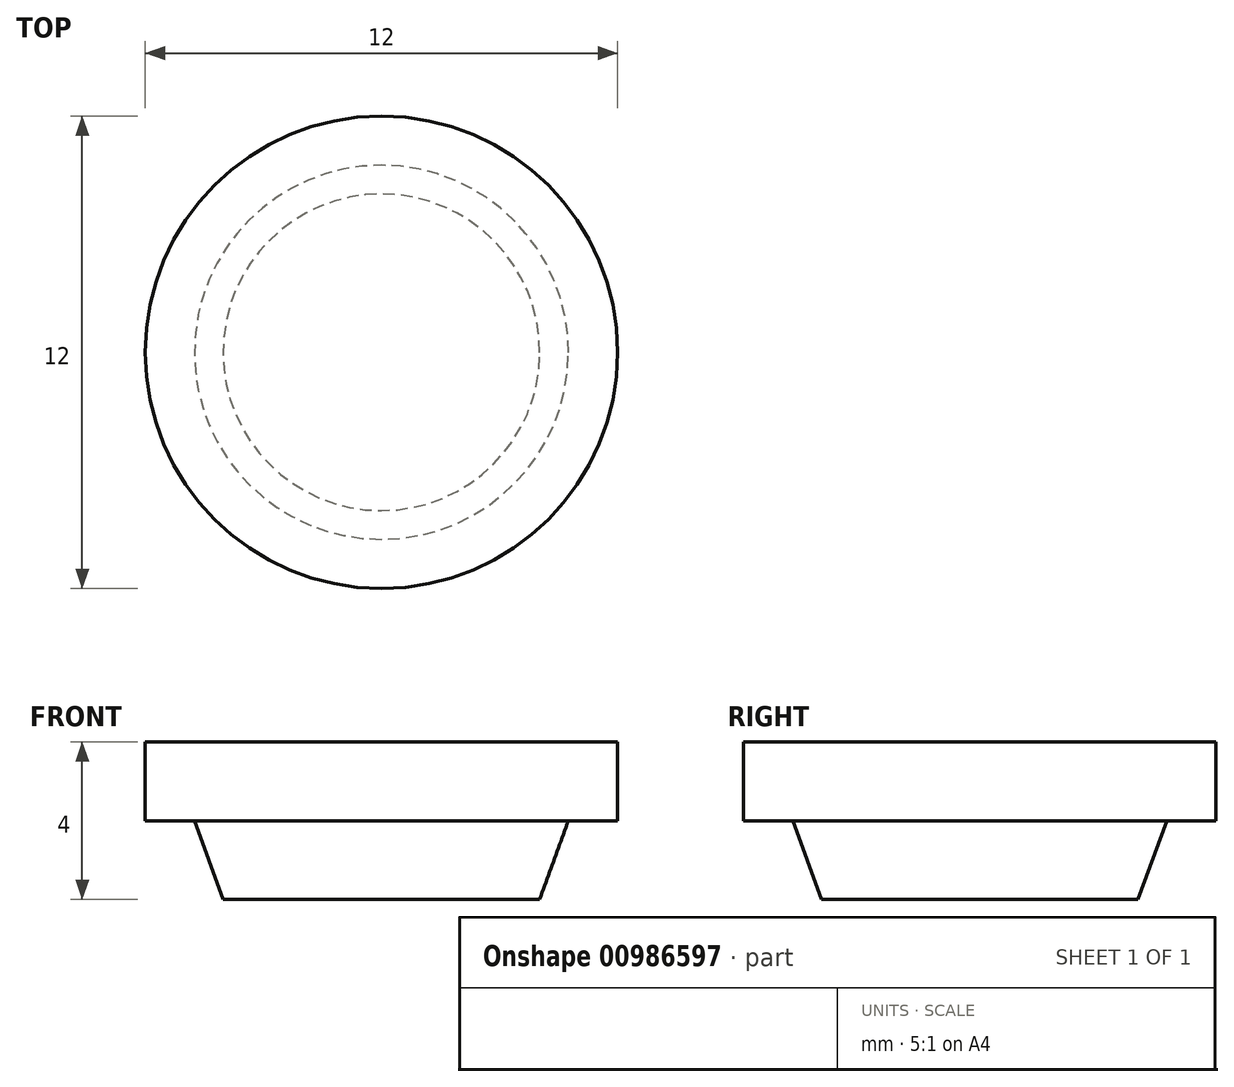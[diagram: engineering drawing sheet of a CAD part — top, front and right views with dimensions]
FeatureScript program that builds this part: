
annotation { "Feature Type Name" : "Feature", "Feature Type Description" : "" }
export const myFeature = defineFeature(function(context is Context, id is Id, definition is map)
    precondition{}
    {
        {
            var Q0;
            Q0=qCreatedBy(makeId("Top.planeOp"),FACE);
            var sketch = newSketch(context, id + "F0", { "sketchPlane" : qUnion([Q0])});
            skCircle(sketch, "E0", {"center": v(0, 0) * mm, "radius": 6 * mm});
            skSolve(sketch);
        }
        {
            var Q0;
            Q0 = qSketchRegion(id + "F0", true);
            extrude(context, id + "F1", {"entities" : qUnion([Q0]), "depth" : 2 * mm, "offsetDistance" : 25 * mm});
        }
        {
            var Q0;
            Q0=qCreatedBy(makeId("Top.planeOp"),FACE);
            var sketch = newSketch(context, id + "F2", { "sketchPlane" : qUnion([Q0])});
            skCircle(sketch, "E1", {"center": v(0, 0) * mm, "radius": 4.75 * mm});
            skSolve(sketch);
        }
        {
            var Q0;
            Q0 = qSketchRegion(id + "F2", true);
            extrude(context, id + "F3", {"entities" : qUnion([Q0]), "operationType" : NewBodyOperationType.ADD, "oppositeDirection" : true, "depth" : 2 * mm, "offsetDistance" : 25 * mm, "hasDraft" : true, "draftAngle" : 20 * degree, "draftPullDirection" : true});
        }
    });
